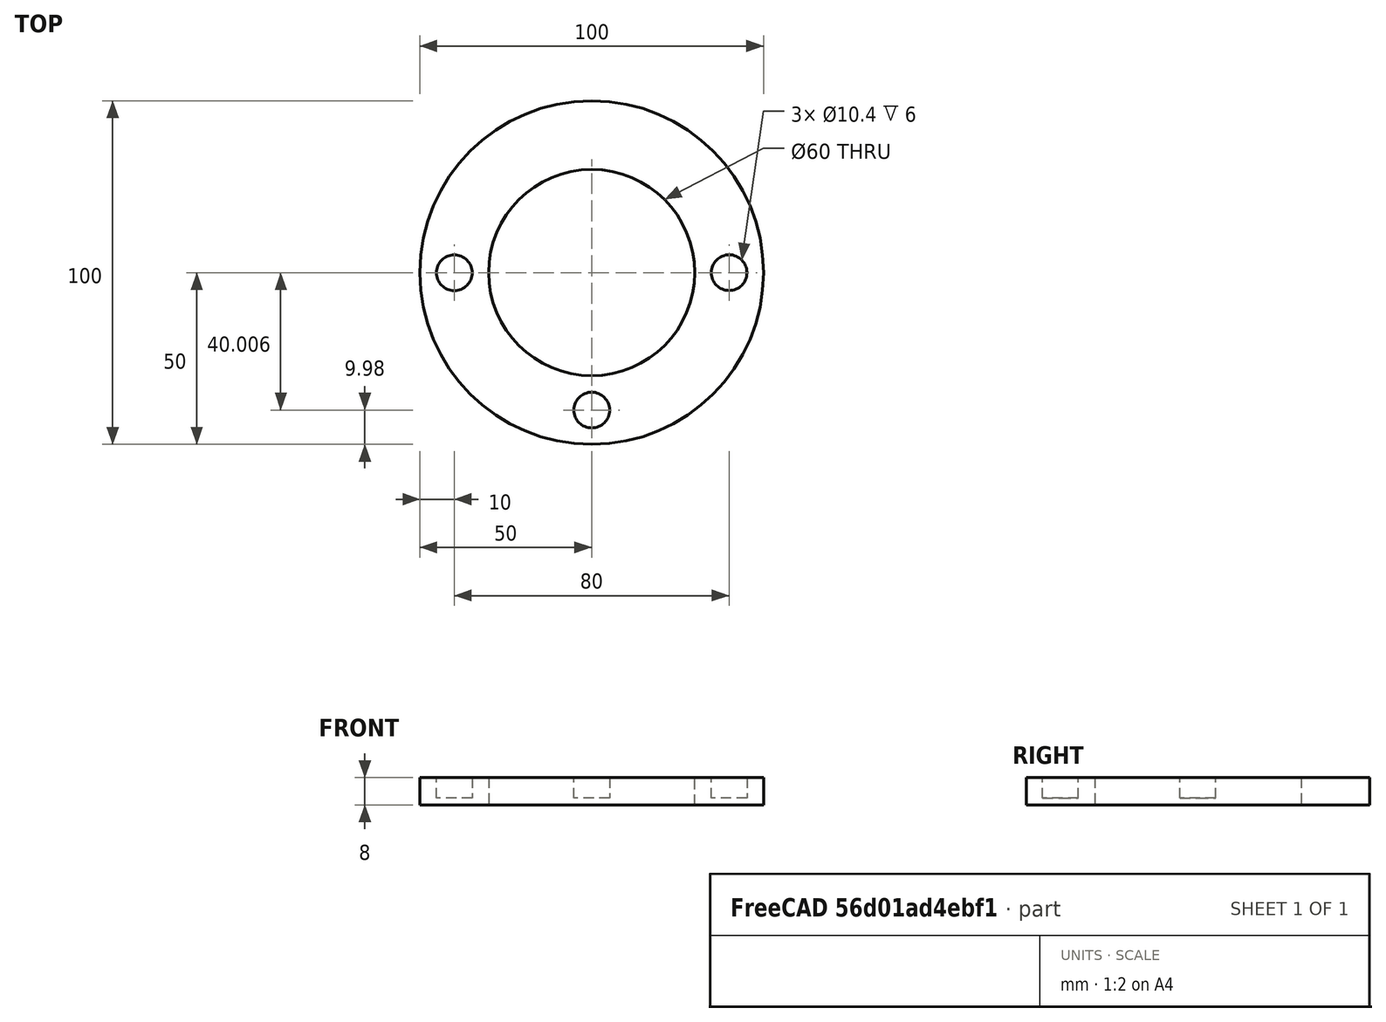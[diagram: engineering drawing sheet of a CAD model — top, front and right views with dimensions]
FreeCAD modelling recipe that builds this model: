
FCSTD DOCUMENT  (FreeCAD 1.0R39319 (Git))
Label: platform0
License: All rights reserved
LicenseURL: https://en.wikipedia.org/wiki/All_rights_reserved
objects: Sketcher::SketchObject×2, PartDesign::Pad×1, PartDesign::Pocket×1, PartDesign::Body×1
note: 11 computed .brp shape members not serialized (recipe doc carries the construction recipe); baked Part::Feature solids carry a one-line shape summary decoded from their .brp

FEATURE [Sketcher::SketchObject] Sketch
  ArcFitTolerance = 1e-06
  AttachmentSupport = -> [XY_Plane]
  FullyConstrained = false
  MakeInternals = false
  MapMode = 5
  sketch-geometry (2):
    g0: Circle CenterX=0 CenterY=0 CenterZ=0 NormalX=0 NormalY=0 NormalZ=1 AngleXU=0 Radius=30
    g1: Circle CenterX=0 CenterY=0 CenterZ=0 NormalX=0 NormalY=0 NormalZ=1 AngleXU=0 Radius=50
  constraints (3):
    c: Diameter(g0) = 60
    c: Coincident(g0,g-1)
    c: Diameter(g1) = 100
FEATURE [PartDesign::Pad] Pad
  Direction = (0,0,1)
  Length = 8
  Length2 = 10
  Profile = -> Sketch
  ReferenceAxis = -> Sketch [N_Axis]
  Refine = true
  Suppressed = false
  Type = 0
FEATURE [Sketcher::SketchObject] Sketch001
  ArcFitTolerance = 1e-06
  AttachmentSupport = -> [Pad]
  FullyConstrained = false
  MakeInternals = false
  MapMode = 5
  Placement = pos=(0,0,8) rot=(0,0,1;0rad)
  sketch-geometry (3):
    g0: Circle CenterX=-40 CenterY=-0.043166 CenterZ=0 NormalX=0 NormalY=0 NormalZ=1 AngleXU=0 Radius=5.2
    g1: Circle CenterX=0 CenterY=-40.0204 CenterZ=0 NormalX=0 NormalY=0 NormalZ=1 AngleXU=0 Radius=5.2
    g2: Circle CenterX=40 CenterY=-0.014127 CenterZ=0 NormalX=0 NormalY=0 NormalZ=1 AngleXU=0 Radius=5.2
  constraints (4):
    c: Diameter(g0) = 10.4
    c: Diameter(g1) = 10.4
    c: PointOnObject(g1,g-2)
    c: Diameter(g2) = 10.4
FEATURE [PartDesign::Pocket] Pocket
  BaseFeature = -> Pad
  Direction = (0,0,-1)
  Length = 6
  Length2 = 5
  Profile = -> Sketch001
  ReferenceAxis = -> Sketch001 [N_Axis]
  Refine = true
  Suppressed = false
  Type = 0
FEATURE [PartDesign::Body] Body
  AllowCompound = false
  Group = -> [Sketch,Pad,Sketch001,Pocket]
  Origin = -> Origin
  Tip = -> Pocket
